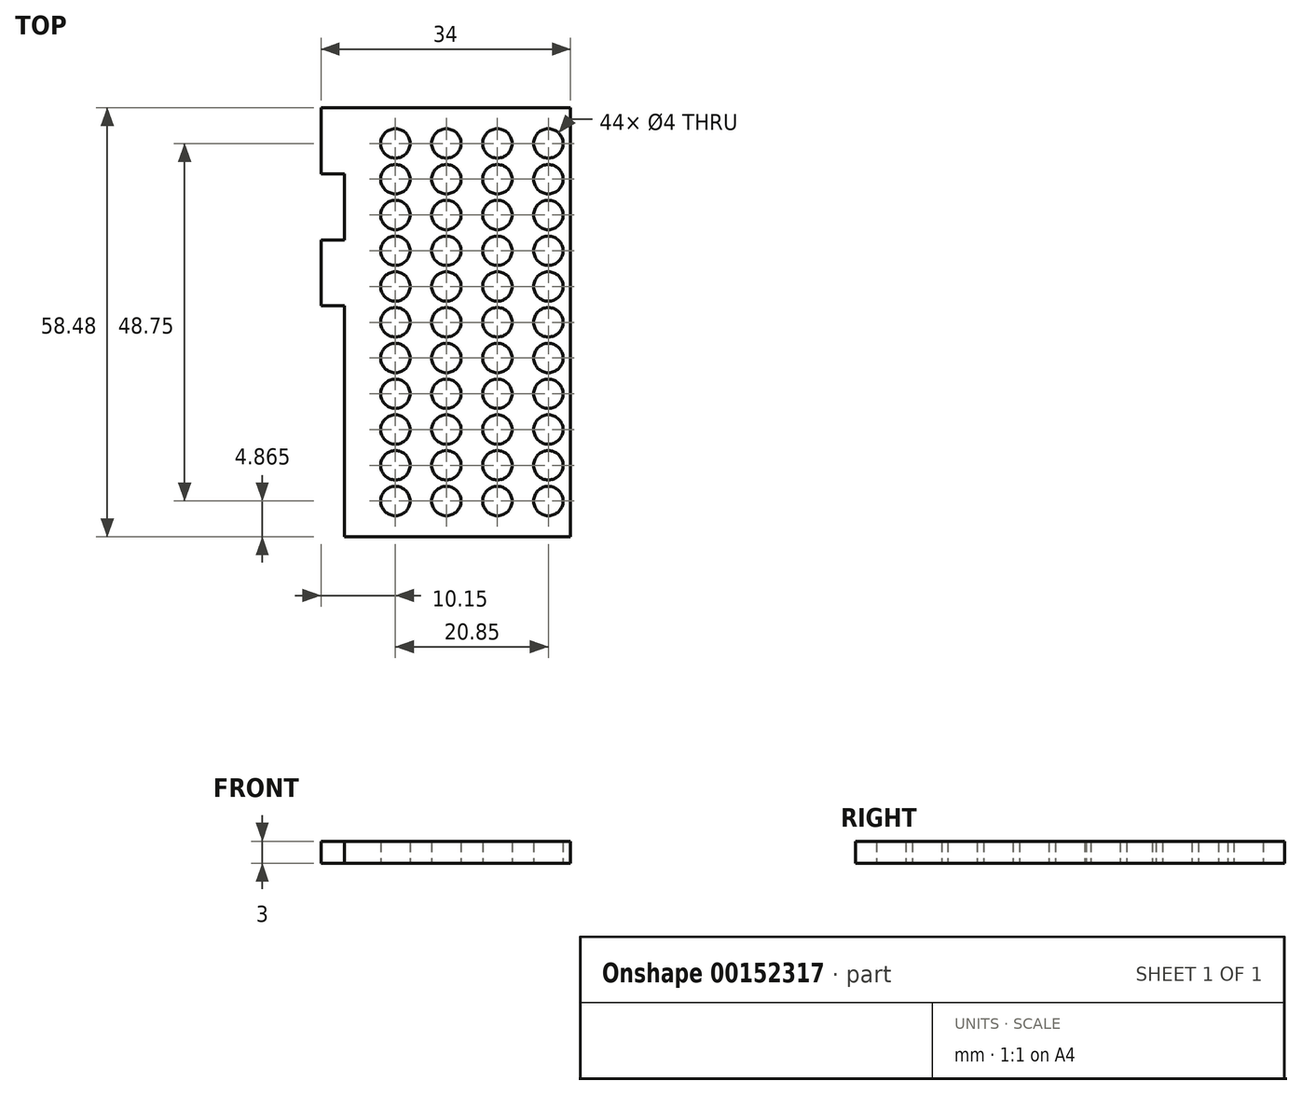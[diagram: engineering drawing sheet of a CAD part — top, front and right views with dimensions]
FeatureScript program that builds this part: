
annotation { "Feature Type Name" : "Feature", "Feature Type Description" : "" }
export const myFeature = defineFeature(function(context is Context, id is Id, definition is map)
    precondition{}
    {
        {
            var Q0;
            Q0=qCreatedBy(makeId("Top.planeOp"),FACE);
            var sketch = newSketch(context, id + "F0", { "sketchPlane" : qUnion([Q0])});
            skLineSegment(sketch, "E0", {"start": v(-20.85, 19.5) * mm, "end": v(-20.85, -18.58) * mm, "construction": true});
            skLineSegment(sketch, "E1.MirrorCS", {"start": v(-20.85, -19.5) * mm, "end": v(-20.85, 18.58) * mm, "construction": true});
            skLineSegment(sketch, "E2", {"start": v(-27.8, -19.5) * mm, "end": v(-27.8, 2.24) * mm, "construction": true});
            skLineSegment(sketch, "E3.MirrorCS", {"start": v(-20.85, 39) * mm, "end": v(-20.85, 0.92) * mm, "construction": true});
            skLineSegment(sketch, "E4.MirrorCS", {"start": v(0, 0) * mm, "end": v(0, 36.5) * mm, "construction": true});
            skLineSegment(sketch, "E5.MirrorCS", {"start": v(-20.85, 0) * mm, "end": v(-20.85, 38.08) * mm, "construction": true});
            skLineSegment(sketch, "E6", {"start": v(-27.8, 24.38) * mm, "end": v(-27.8, 24.37) * mm, "construction": true});
            skLineSegment(sketch, "E7", {"start": v(-27.8, 24.38) * mm, "end": v(-27.8, 24.37) * mm});
            skLineSegment(sketch, "E8", {"start": v(-27.8, 29.24) * mm, "end": v(-31, 29.24) * mm});
            skLineSegment(sketch, "E9", {"start": v(-31, 29.24) * mm, "end": v(-31, 20.24) * mm});
            skLineSegment(sketch, "E10", {"start": v(-31, 20.24) * mm, "end": v(-27.8, 20.24) * mm});
            skLineSegment(sketch, "E11.trimOffspring", {"start": v(-27.8, 20.24) * mm, "end": v(-27.8, 11.24) * mm, "construction": true});
            skLineSegment(sketch, "E12.trimOffspring", {"start": v(-27.8, 20.24) * mm, "end": v(-27.8, 11.24) * mm});
            skLineSegment(sketch, "E13", {"start": v(-27.8, 20.24) * mm, "end": v(-27.8, 16.32) * mm, "construction": true});
            skLineSegment(sketch, "E14", {"start": v(-27.8, 11.24) * mm, "end": v(-31, 11.24) * mm});
            skLineSegment(sketch, "E15", {"start": v(-31, 11.24) * mm, "end": v(-31, 2.24) * mm});
            skLineSegment(sketch, "E16", {"start": v(-31, 2.24) * mm, "end": v(-27.8, 2.24) * mm});
            skLineSegment(sketch, "E17.trimOffspring", {"start": v(-27.8, 11.24) * mm, "end": v(-27.8, 19.5) * mm, "construction": true});
            skLineSegment(sketch, "E18.trimOffspring", {"start": v(-27.8, 2.24) * mm, "end": v(-27.8, -19.5) * mm, "construction": true});
            skLineSegment(sketch, "E19.trimOffspring", {"start": v(-27.8, 2.24) * mm, "end": v(-27.8, -19.5) * mm});
            skCircle(sketch, "E20.MirrorC", {"center": v(-6.95, 24.38) * mm, "radius": 2 * mm});
            skCircle(sketch, "E21.MirrorC", {"center": v(-13.9, 0) * mm, "radius": 2 * mm});
            skCircle(sketch, "E22.MirrorC", {"center": v(-6.95, 14.63) * mm, "radius": 2 * mm});
            skCircle(sketch, "E23.MirrorC", {"center": v(-6.95, 0) * mm, "radius": 2 * mm});
            skCircle(sketch, "E24.MirrorC", {"center": v(-6.95, 19.5) * mm, "radius": 2 * mm});
            skCircle(sketch, "E25.MirrorC", {"center": v(-13.9, 14.63) * mm, "radius": 2 * mm});
            skCircle(sketch, "E26.MirrorC", {"center": v(-6.95, -14.62) * mm, "radius": 2 * mm});
            skCircle(sketch, "E27.MirrorC", {"center": v(-13.9, -4.88) * mm, "radius": 2 * mm});
            skCircle(sketch, "E28.MirrorC", {"center": v(-13.9, 9.75) * mm, "radius": 2 * mm});
            skCircle(sketch, "E29.MirrorC", {"center": v(-13.9, 4.88) * mm, "radius": 2 * mm});
            skCircle(sketch, "E30.MirrorC", {"center": v(-13.9, 19.5) * mm, "radius": 2 * mm});
            skCircle(sketch, "E31.MirrorC", {"center": v(-6.95, -9.75) * mm, "radius": 2 * mm});
            skCircle(sketch, "E32.MirrorC", {"center": v(-13.9, 24.38) * mm, "radius": 2 * mm});
            skCircle(sketch, "E33.MirrorC", {"center": v(-6.95, 9.75) * mm, "radius": 2 * mm});
            skCircle(sketch, "E34.MirrorC", {"center": v(-13.9, -14.62) * mm, "radius": 2 * mm});
            skCircle(sketch, "E35.MirrorC", {"center": v(-13.9, -9.75) * mm, "radius": 2 * mm});
            skCircle(sketch, "E36.MirrorC", {"center": v(-6.95, 4.88) * mm, "radius": 2 * mm});
            skCircle(sketch, "E37.MirrorC", {"center": v(-6.95, -4.88) * mm, "radius": 2 * mm});
            skLineSegment(sketch, "E38", {"start": v(-6.95, 29.24) * mm, "end": v(0, 29.24) * mm, "construction": true});
            skLineSegment(sketch, "E39", {"start": v(-3.47, 29.24) * mm, "end": v(-3.47, -19.5) * mm, "construction": true});
            skCircle(sketch, "E40.MirrorC", {"center": v(0, 24.38) * mm, "radius": 2 * mm});
            skCircle(sketch, "E41.MirrorC", {"center": v(0, -4.88) * mm, "radius": 2 * mm});
            skCircle(sketch, "E42.MirrorC", {"center": v(0, -14.62) * mm, "radius": 2 * mm});
            skCircle(sketch, "E43.MirrorC", {"center": v(0, -9.75) * mm, "radius": 2 * mm});
            skCircle(sketch, "E44.MirrorC", {"center": v(0, 14.63) * mm, "radius": 2 * mm});
            skCircle(sketch, "E45.MirrorC", {"center": v(0, 0) * mm, "radius": 2 * mm});
            skCircle(sketch, "E46.MirrorC", {"center": v(0, 9.75) * mm, "radius": 2 * mm});
            skCircle(sketch, "E47.MirrorC", {"center": v(0, 19.5) * mm, "radius": 2 * mm});
            skCircle(sketch, "E48.MirrorC", {"center": v(0, 4.88) * mm, "radius": 2 * mm});
            skCircle(sketch, "E49.MirrorC", {"center": v(-20.85, -4.88) * mm, "radius": 2 * mm});
            skCircle(sketch, "E50.MirrorC", {"center": v(-20.85, 9.75) * mm, "radius": 2 * mm});
            skCircle(sketch, "E51.MirrorC", {"center": v(-20.85, 4.88) * mm, "radius": 2 * mm});
            skCircle(sketch, "E52.MirrorC", {"center": v(-20.85, -9.75) * mm, "radius": 2 * mm});
            skCircle(sketch, "E53.MirrorC", {"center": v(-20.85, 0) * mm, "radius": 2 * mm});
            skCircle(sketch, "E54.MirrorC", {"center": v(-20.85, 14.63) * mm, "radius": 2 * mm});
            skCircle(sketch, "E55.MirrorC", {"center": v(-20.85, 19.5) * mm, "radius": 2 * mm});
            skCircle(sketch, "E56.MirrorC", {"center": v(-20.85, 24.38) * mm, "radius": 2 * mm});
            skCircle(sketch, "E57.MirrorC", {"center": v(-20.85, -14.62) * mm, "radius": 2 * mm});
            skLineSegment(sketch, "E58", {"start": v(3, 29.24) * mm, "end": v(3, -19.5) * mm});
            skLineSegment(sketch, "E59", {"start": v(-27.8, 29.24) * mm, "end": v(3, 29.24) * mm});
            skLineSegment(sketch, "E60", {"start": v(-27.8, 29.24) * mm, "end": v(-27.8, -29.23) * mm, "construction": true});
            skLineSegment(sketch, "E61", {"start": v(3, 0) * mm, "end": v(-27.8, 0) * mm, "construction": true});
            skLineSegment(sketch, "E62", {"start": v(-27.8, -19.5) * mm, "end": v(-27.8, -29.23) * mm});
            skCircle(sketch, "E63.MirrorC", {"center": v(-13.9, -19.5) * mm, "radius": 2 * mm});
            skCircle(sketch, "E64.MirrorC", {"center": v(-20.85, -19.5) * mm, "radius": 2 * mm});
            skCircle(sketch, "E65.MirrorC", {"center": v(-6.95, -19.5) * mm, "radius": 2 * mm});
            skLineSegment(sketch, "E66.MirrorCS", {"start": v(3, -29.24) * mm, "end": v(3, 19.5) * mm});
            skCircle(sketch, "E67.MirrorC", {"center": v(0, -19.5) * mm, "radius": 2 * mm});
            skCircle(sketch, "E68.MirrorC", {"center": v(0, -24.37) * mm, "radius": 2 * mm});
            skCircle(sketch, "E69.MirrorC", {"center": v(-6.95, -24.37) * mm, "radius": 2 * mm});
            skCircle(sketch, "E70.MirrorC", {"center": v(-13.9, -24.37) * mm, "radius": 2 * mm});
            skCircle(sketch, "E71.MirrorC", {"center": v(-20.85, -24.37) * mm, "radius": 2 * mm});
            skLineSegment(sketch, "E72", {"start": v(-20.85, -24.37) * mm, "end": v(-27.8, -24.37) * mm, "construction": true});
            skLineSegment(sketch, "E73", {"start": v(-27.8, -24.37) * mm, "end": v(-27.8, -29.23) * mm, "construction": true});
            skLineSegment(sketch, "E74", {"start": v(-27.8, -29.23) * mm, "end": v(3, -29.24) * mm});
            skSolve(sketch);
        }
        {
            var Q0;
            Q0=qSketchRegion(id+"F0",true);
            extrude(context, id + "F1", {"entities" : qUnion([Q0]), "endBound" : BoundingType.SYMMETRIC, "depth" : 3 * mm});
        }
    });
